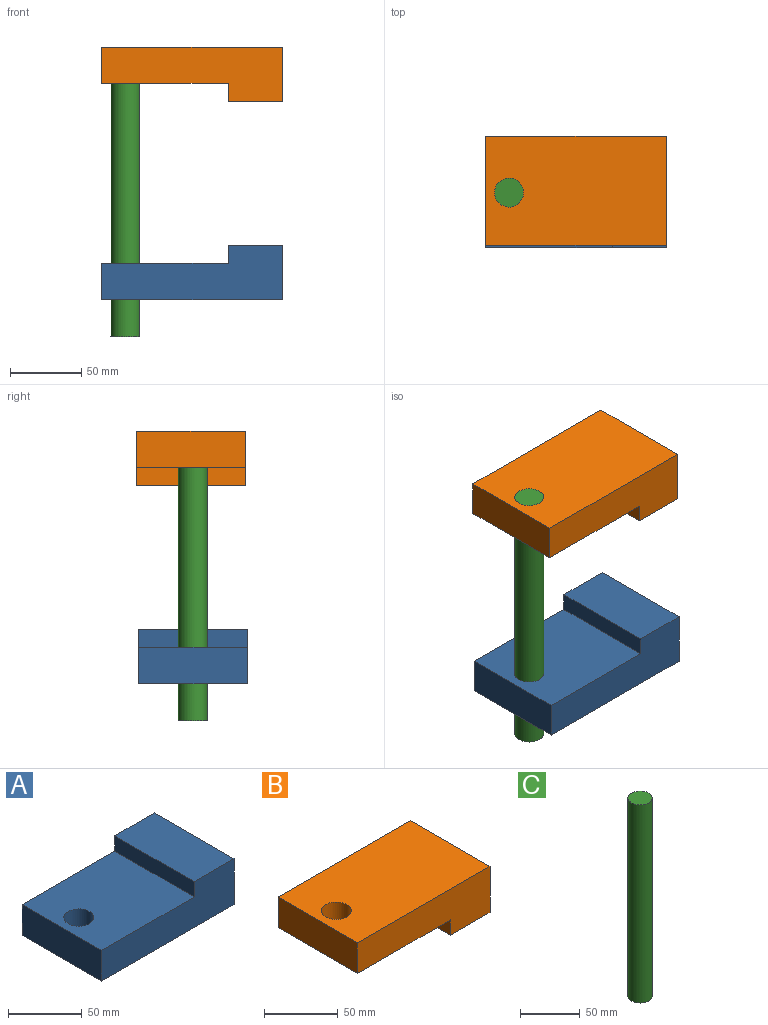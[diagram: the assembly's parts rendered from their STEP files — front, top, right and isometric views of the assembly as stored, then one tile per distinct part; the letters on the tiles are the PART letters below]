
ASSEMBLY  parts=3 mates=2
PART A: 9 faces, bbox 127x76.2x38.1 mm
  f0: plane 76.2x38.1mm, normal (1,0,0), area 2903.2mm2, adj f1,f5,f6,f7
  f1: plane 76.2x38.1mm, normal (0,0,1), area 2903.2mm2, adj f0,f2,f6,f7
  f2: plane 76.2x12.7mm, normal (-1,0,0), area 967.7mm2, adj f1,f3,f6,f7
  f3: plane 88.9x76.2mm, normal (0,0,1), area 6449.9mm2, adj f2,f4,f6,f7,f8
  f4: plane 76.2x25.4mm, normal (-1,0,0), area 1935.5mm2, adj f3,f5,f6,f7
  f5: plane 127x76.2mm, normal (0,0,-1), area 9353.1mm2, adj f0,f4,f6,f7,f8
  f6: plane 127x38.1mm, normal (0,-1,0), area 3709.7mm2, adj f0,f1,f2,f3,f4,f5
  f7: plane 127x38.1mm, normal (0,1,0), area 3709.7mm2, adj f0,f1,f2,f3,f4,f5
  f8: cylinder r=10.16mm len=25.4mm, axis (0,0,-1), area 1621.5mm2, adj f3,f5
PART B: 9 faces, bbox 127x76.2x38.1 mm
  f0: plane 88.9x76.2mm, normal (0,0,-1), area 6449.9mm2, adj f1,f5,f6,f7,f8
  f1: plane 76.2x12.7mm, normal (-1,0,0), area 967.7mm2, adj f0,f2,f6,f7
  f2: plane 76.2x38.1mm, normal (0,0,-1), area 2903.2mm2, adj f1,f3,f6,f7
  f3: plane 76.2x38.1mm, normal (1,0,0), area 2903.2mm2, adj f2,f4,f6,f7
  f4: plane 127x76.2mm, normal (0,0,1), area 9353.1mm2, adj f3,f5,f6,f7,f8
  f5: plane 76.2x25.4mm, normal (-1,0,0), area 1935.5mm2, adj f0,f4,f6,f7
  f6: plane 127x38.1mm, normal (0,-1,0), area 3709.7mm2, adj f0,f1,f2,f3,f4,f5
  f7: plane 127x38.1mm, normal (0,1,0), area 3709.7mm2, adj f0,f1,f2,f3,f4,f5
  f8: cylinder r=10.16mm len=25.4mm, axis (0,0,1), area 1621.5mm2, adj f0,f4
PART C: 3 faces, bbox 20.3x20.3x203.2 mm
  f0: cylinder r=10.16mm len=203.2mm, axis (0,0,1), area 12971.7mm2, adj f1,f2
  f1: plane 20.32x20.32mm, normal (0,0,-1), area 324.3mm2, adj f0
  f2: plane 20.32x20.32mm, normal (0,0,1), area 324.3mm2, adj f0
PLACE A t=(-52.04,-168.65,-137.43)mm
PLACE B t=(-43.6,-167.25,-49.68)mm
PLACE C t=(28.52,-190.65,-7.46)mm
MATE cylindrical C.f0 <-> B.f8  axis (0,0,1) through (-89.61,-206.62,-7.46)mm
MATE cylindrical A.f8 <-> C.f0  axis (0,0,1) through (-89.61,-206.62,-159.1)mm
